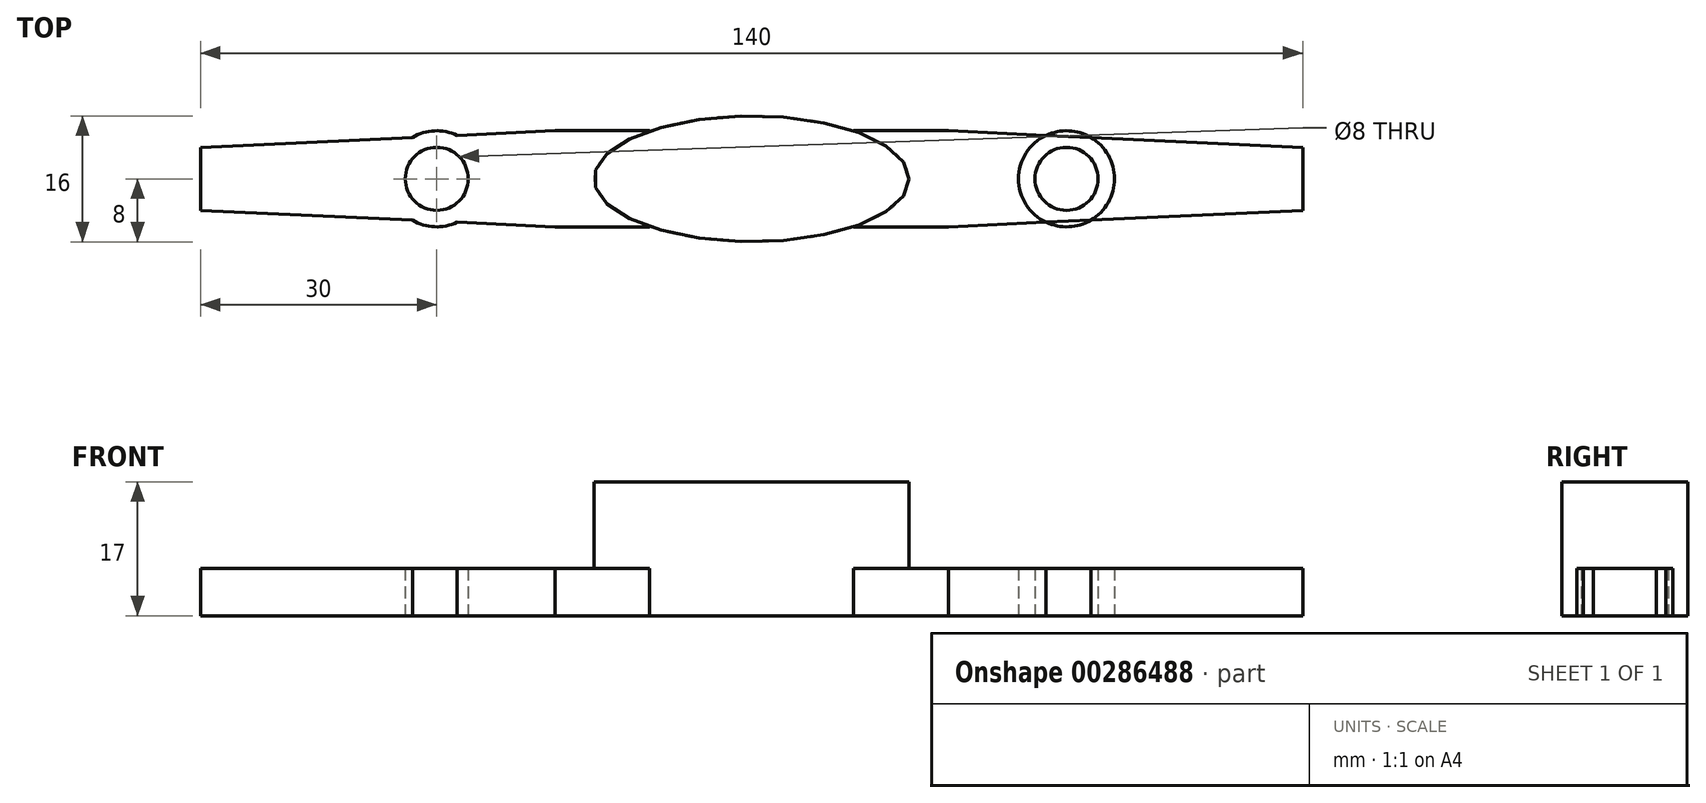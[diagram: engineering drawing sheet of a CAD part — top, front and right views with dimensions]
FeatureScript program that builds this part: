
annotation { "Feature Type Name" : "Feature", "Feature Type Description" : "" }
export const myFeature = defineFeature(function(context is Context, id is Id, definition is map)
    precondition{}
    {
        {
            var Q0;
            Q0=qCreatedBy(makeId("Top.planeOp"),FACE);
            var sketch = newSketch(context, id + "F0", { "sketchPlane" : qUnion([Q0])});
            skEllipse(sketch, "E0", {"center": v(0, 0) * mm, "majorRadius": 20 * mm, "minorRadius": 8 * mm, "majorAxis": v(1, 0)});
            skLineSegment(sketch, "E1", {"start": v(-70, 0) * mm, "end": v(-70, 4) * mm});
            skLineSegment(sketch, "E2.MirrorCS", {"start": v(-70, 0) * mm, "end": v(-70, -4) * mm});
            skLineSegment(sketch, "E3.MirrorCS", {"start": v(70, 0) * mm, "end": v(70, 4) * mm});
            skLineSegment(sketch, "E4.MirrorCS", {"start": v(70, 0) * mm, "end": v(70, -4) * mm});
            skLineSegment(sketch, "E5", {"start": v(-70, 4) * mm, "end": v(-25, 6.1) * mm});
            skLineSegment(sketch, "E6", {"start": v(-25, 6.1) * mm, "end": v(-12.94, 6.1) * mm});
            skLineSegment(sketch, "E7.MirrorCS", {"start": v(-70, -4) * mm, "end": v(-25, -6.1) * mm});
            skLineSegment(sketch, "E8.MirrorCS", {"start": v(-25, -6.1) * mm, "end": v(-12.94, -6.1) * mm});
            skLineSegment(sketch, "E9.MirrorCS", {"start": v(25, 6.1) * mm, "end": v(12.94, 6.1) * mm});
            skLineSegment(sketch, "E10.MirrorCS", {"start": v(25, -6.1) * mm, "end": v(12.94, -6.1) * mm});
            skLineSegment(sketch, "E11.MirrorCS", {"start": v(70, -4) * mm, "end": v(25, -6.1) * mm});
            skLineSegment(sketch, "E12.MirrorCS", {"start": v(70, 4) * mm, "end": v(25, 6.1) * mm});
            skCircle(sketch, "E13", {"center": v(-40, 0) * mm, "radius": 4 * mm});
            skCircle(sketch, "E14.MirrorC", {"center": v(40, 0) * mm, "radius": 4 * mm});
            skCircle(sketch, "E15", {"center": v(-40, 0) * mm, "radius": 6.1 * mm});
            skCircle(sketch, "E16.MirrorC", {"center": v(40, 0) * mm, "radius": 6.1 * mm});
            skSolve(sketch);
        }
        {
            var Q0;
            {var subQ5=sQuery(id+"F0.wireOp",EDGE,"E1");Q0=makeQuery(id+"F0.imprint","IMPRINT",FACE,{"disambiguationData":[TD([[makeQuery(id+"F0.imprint","IMPRINT",EDGE,{"derivedFrom":subQ5}),-1.0]])]});}
            var Q1;
            {var subQ5=sQuery(id+"F0.wireOp",EDGE,"E3.MirrorCS");Q1=makeQuery(id+"F0.imprint","IMPRINT",FACE,{"disambiguationData":[TD([[makeQuery(id+"F0.imprint","IMPRINT",EDGE,{"derivedFrom":subQ5}),1.0]])]});}
            var Q2;
            {var subQ0=sQuery(id+"F0.wireOp",EDGE,"E15");var subQ1=sQuery(id+"F0.wireOp",EDGE,"E5");var subQ2=makeQuery(id+"F0.imprint","INTERSECT",VERTEX,{"disambiguationData":[OD(0.0)],"derivedFrom":[subQ1,subQ0]});Q2=makeQuery(id+"F0.imprint","IMPRINT",FACE,{"disambiguationData":[TD([[makeQuery(id+"F0.imprint","IMPRINT",EDGE,{"disambiguationData":[TD([[subQ2,-1.0]])],"derivedFrom":subQ1}),1.0]])]});}
            var Q3;
            {var subQ0=sQuery(id+"F0.wireOp",EDGE,"E15");var subQ1=sQuery(id+"F0.wireOp",EDGE,"E7.MirrorCS");var subQ2=makeQuery(id+"F0.imprint","INTERSECT",VERTEX,{"disambiguationData":[OD(0.0)],"derivedFrom":[subQ1,subQ0]});Q3=makeQuery(id+"F0.imprint","IMPRINT",FACE,{"disambiguationData":[TD([[makeQuery(id+"F0.imprint","IMPRINT",EDGE,{"disambiguationData":[TD([[subQ2,-1.0]])],"derivedFrom":subQ1}),-1.0]])]});}
            var Q4;
            {var subQ0=sQuery(id+"F0.wireOp",EDGE,"E16.MirrorC");var subQ1=sQuery(id+"F0.wireOp",EDGE,"E11.MirrorCS");var subQ2=makeQuery(id+"F0.imprint","INTERSECT",VERTEX,{"disambiguationData":[OD(0.0)],"derivedFrom":[subQ1,subQ0]});Q4=makeQuery(id+"F0.imprint","IMPRINT",FACE,{"disambiguationData":[TD([[makeQuery(id+"F0.imprint","IMPRINT",EDGE,{"disambiguationData":[TD([[subQ2,-1.0]])],"derivedFrom":subQ1}),1.0]])]});}
            var Q5;
            {var subQ0=sQuery(id+"F0.wireOp",EDGE,"E16.MirrorC");var subQ1=sQuery(id+"F0.wireOp",EDGE,"E12.MirrorCS");var subQ2=makeQuery(id+"F0.imprint","INTERSECT",VERTEX,{"disambiguationData":[OD(0.0)],"derivedFrom":[subQ1,subQ0]});Q5=makeQuery(id+"F0.imprint","IMPRINT",FACE,{"disambiguationData":[TD([[makeQuery(id+"F0.imprint","IMPRINT",EDGE,{"disambiguationData":[TD([[subQ2,-1.0]])],"derivedFrom":subQ1}),-1.0]])]});}
            var Q6;
            {var subQ4=sQuery(id+"F0.wireOp",EDGE,"E6");Q6=makeQuery(id+"F0.imprint","IMPRINT",FACE,{"disambiguationData":[TD([[makeQuery(id+"F0.imprint","IMPRINT",EDGE,{"derivedFrom":subQ4}),-1.0]])]});}
            var Q7;
            {var subQ4=sQuery(id+"F0.wireOp",EDGE,"E9.MirrorCS");Q7=makeQuery(id+"F0.imprint","IMPRINT",FACE,{"disambiguationData":[TD([[makeQuery(id+"F0.imprint","IMPRINT",EDGE,{"derivedFrom":subQ4}),1.0]])]});}
            var Q8;
            Q8=makeQuery(id+"F0.imprint","IMPRINT",FACE,{"disambiguationData":[TD([[makeQuery(id+"F0.imprint","IMPRINT",EDGE,{"derivedFrom":sQuery(id+"F0.wireOp",EDGE,"E13")}),-1.0]])]});
            var Q9;
            Q9=makeQuery(id+"F0.imprint","IMPRINT",FACE,{"disambiguationData":[TD([[makeQuery(id+"F0.imprint","IMPRINT",EDGE,{"derivedFrom":sQuery(id+"F0.wireOp",EDGE,"E14.MirrorC")}),1.0]])]});
            extrude(context, id + "F1", {"entities" : qUnion([Q0, Q1, Q2, Q3, Q4, Q5, Q6, Q7, Q8, Q9]), "depth" : 6 * mm, "offsetDistance" : 25 * mm});
        }
        {
            var Q0;
            {var subQ0=sQuery(id+"F0.wireOp",EDGE,"E0");var subQ1=makeQuery(id+"F0.imprint","INTERSECT",VERTEX,{"derivedFrom":[subQ0,sQuery(id+"F0.wireOp",EDGE,"E6")]});Q0=makeQuery(id+"F0.imprint","IMPRINT",FACE,{"disambiguationData":[TD([[makeQuery(id+"F0.imprint","IMPRINT",EDGE,{"disambiguationData":[TD([[subQ1,1.0]])],"derivedFrom":subQ0}),1.0]])]});}
            extrude(context, id + "F2", {"entities" : qUnion([Q0]), "operationType" : NewBodyOperationType.ADD, "depth" : 17 * mm, "offsetDistance" : 25 * mm});
        }
    });
